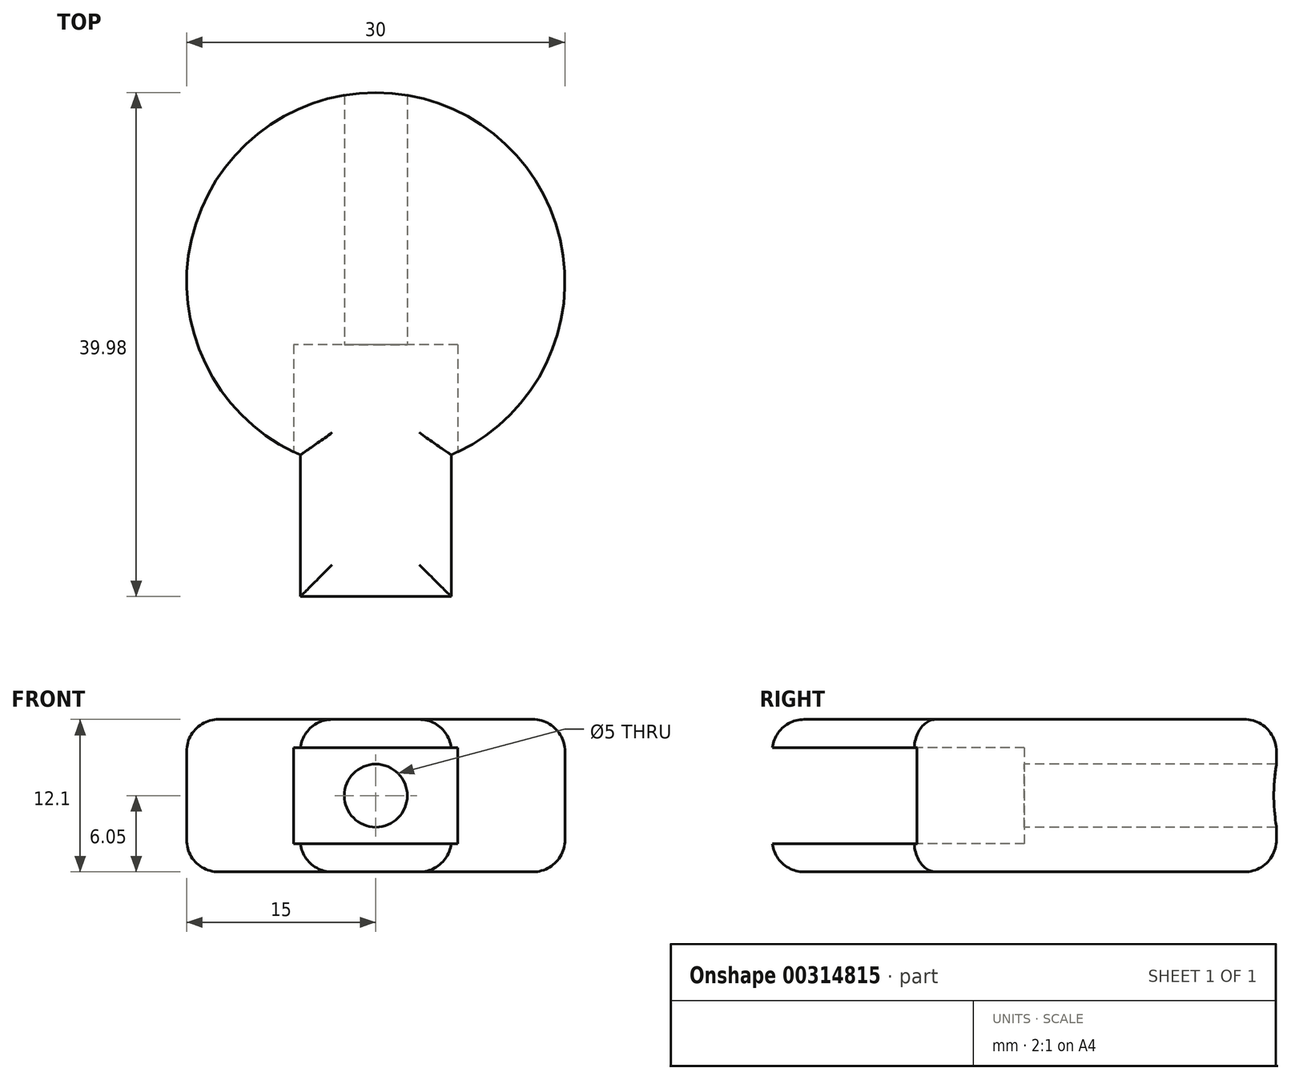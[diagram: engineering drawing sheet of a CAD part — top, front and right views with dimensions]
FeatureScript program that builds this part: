
annotation { "Feature Type Name" : "Feature", "Feature Type Description" : "" }
export const myFeature = defineFeature(function(context is Context, id is Id, definition is map)
    precondition{}
    {
        {
            var Q0;
            Q0=qCreatedBy(makeId("Top.planeOp"),FACE);
            var sketch = newSketch(context, id + "F0", { "sketchPlane" : qUnion([Q0])});
            skArc(sketch, "E0", {"start": v(6, -13.75) * mm, "mid": v(0, 15) * mm, "end": v(-6, -13.75) * mm});
            skLineSegment(sketch, "E1", {"start": v(0, 0) * mm, "end": v(0, -25) * mm, "construction": true});
            skLineSegment(sketch, "E2", {"start": v(0, -25) * mm, "end": v(6, -25) * mm});
            skLineSegment(sketch, "E3", {"start": v(0, -25) * mm, "end": v(-6, -25) * mm});
            skLineSegment(sketch, "E4", {"start": v(-6, -25) * mm, "end": v(-6, -13.75) * mm});
            skLineSegment(sketch, "E5", {"start": v(6, -25) * mm, "end": v(6, -13.75) * mm});
            skSolve(sketch);
        }
        {
            var Q0;
            Q0 = qSketchRegion(id + "F0", true);
            extrude(context, id + "F1", {"entities" : qUnion([Q0]), "depth" : 12.1 * mm});
        }
        {
            var Q0;
            Q0=makeQuery(id+"F1.opExtrude","CAP_FACE",FACE,{"disambiguationData":[OSD([sQuery(id+"F0.wireOp",EDGE,"E0"),sQuery(id+"F0.wireOp",EDGE,"E2"),sQuery(id+"F0.wireOp",EDGE,"E3"),sQuery(id+"F0.wireOp",EDGE,"E4"),sQuery(id+"F0.wireOp",EDGE,"E5")])],"isStart":false});
            var Q1;
            Q1=makeQuery(id+"F1.opExtrude","CAP_FACE",FACE,{"disambiguationData":[OSD([sQuery(id+"F0.wireOp",EDGE,"E0"),sQuery(id+"F0.wireOp",EDGE,"E2"),sQuery(id+"F0.wireOp",EDGE,"E3"),sQuery(id+"F0.wireOp",EDGE,"E4"),sQuery(id+"F0.wireOp",EDGE,"E5")])],"isStart":true});
            fillet(context, id + "F2", {"entities" : qUnion([Q0, Q1]), "radius" : 2.54 * mm, "tangentPropagation" : true, "allowEdgeOverflow" : false});
        }
        {
            var Q0;
            Q0=makeQuery(id+"F1.opExtrude","SWEPT_FACE",FACE,{"disambiguationData":[OSD([sQuery(id+"F0.wireOp",EDGE,"E2"),sQuery(id+"F0.wireOp",EDGE,"E3")])]});
            var sketch = newSketch(context, id + "F3", { "sketchPlane" : qUnion([Q0])});
            skLineSegment(sketch, "E6", {"start": v(6, 9.56) * mm, "end": v(-6, 2.54) * mm, "construction": true});
            skLineSegment(sketch, "E7", {"start": v(-6, 2.54) * mm, "end": v(-6, 9.56) * mm, "construction": true});
            skLineSegment(sketch, "E8", {"start": v(-6, 9.56) * mm, "end": v(6, 2.54) * mm, "construction": true});
            skLineSegment(sketch, "E9.bottom", {"start": v(6.51, 9.86) * mm, "end": v(-6.51, 9.86) * mm});
            skLineSegment(sketch, "E9.top", {"start": v(6.51, 2.24) * mm, "end": v(-6.51, 2.24) * mm});
            skLineSegment(sketch, "E9.left", {"start": v(6.51, 9.86) * mm, "end": v(6.51, 2.24) * mm});
            skLineSegment(sketch, "E9.right", {"start": v(-6.51, 9.86) * mm, "end": v(-6.51, 2.24) * mm});
            skPoint(sketch, "E9.middle", {"position": v(0, 6.05) * mm});
            skSolve(sketch);
        }
        {
            var Q0;
            Q0 = qSketchRegion(id + "F3", true);
            extrude(context, id + "F4", {"entities" : qUnion([Q0]), "operationType" : NewBodyOperationType.REMOVE, "oppositeDirection" : true, "depth" : 20 * mm});
        }
        {
            var Q0;
            Q0=makeQuery(id+"F4.boolean.opBoolean","COPY",FACE,{"derivedFrom":makeQuery(id+"F4.opExtrude","CAP_FACE",FACE,{"disambiguationData":[OSD([sQuery(id+"F3.wireOp",EDGE,"E9.bottom"),sQuery(id+"F3.wireOp",EDGE,"E9.top"),sQuery(id+"F3.wireOp",EDGE,"E9.left"),sQuery(id+"F3.wireOp",EDGE,"E9.right")])],"isStart":false})});
            var sketch = newSketch(context, id + "F5", { "sketchPlane" : qUnion([Q0])});
            skLineSegment(sketch, "E10", {"start": v(-6.51, 9.86) * mm, "end": v(6.51, 2.24) * mm, "construction": true});
            skLineSegment(sketch, "E11", {"start": v(6.51, 2.24) * mm, "end": v(6.51, 9.86) * mm, "construction": true});
            skLineSegment(sketch, "E12", {"start": v(6.51, 9.86) * mm, "end": v(-6.51, 2.24) * mm, "construction": true});
            skCircle(sketch, "E13", {"center": v(0, 6.05) * mm, "radius": 2.5 * mm});
            skSolve(sketch);
        }
        {
            var Q0;
            Q0 = qSketchRegion(id + "F5", true);
            extrude(context, id + "F6", {"entities" : qUnion([Q0]), "operationType" : NewBodyOperationType.REMOVE, "oppositeDirection" : true, "depth" : 25.4 * mm});
        }
    });
